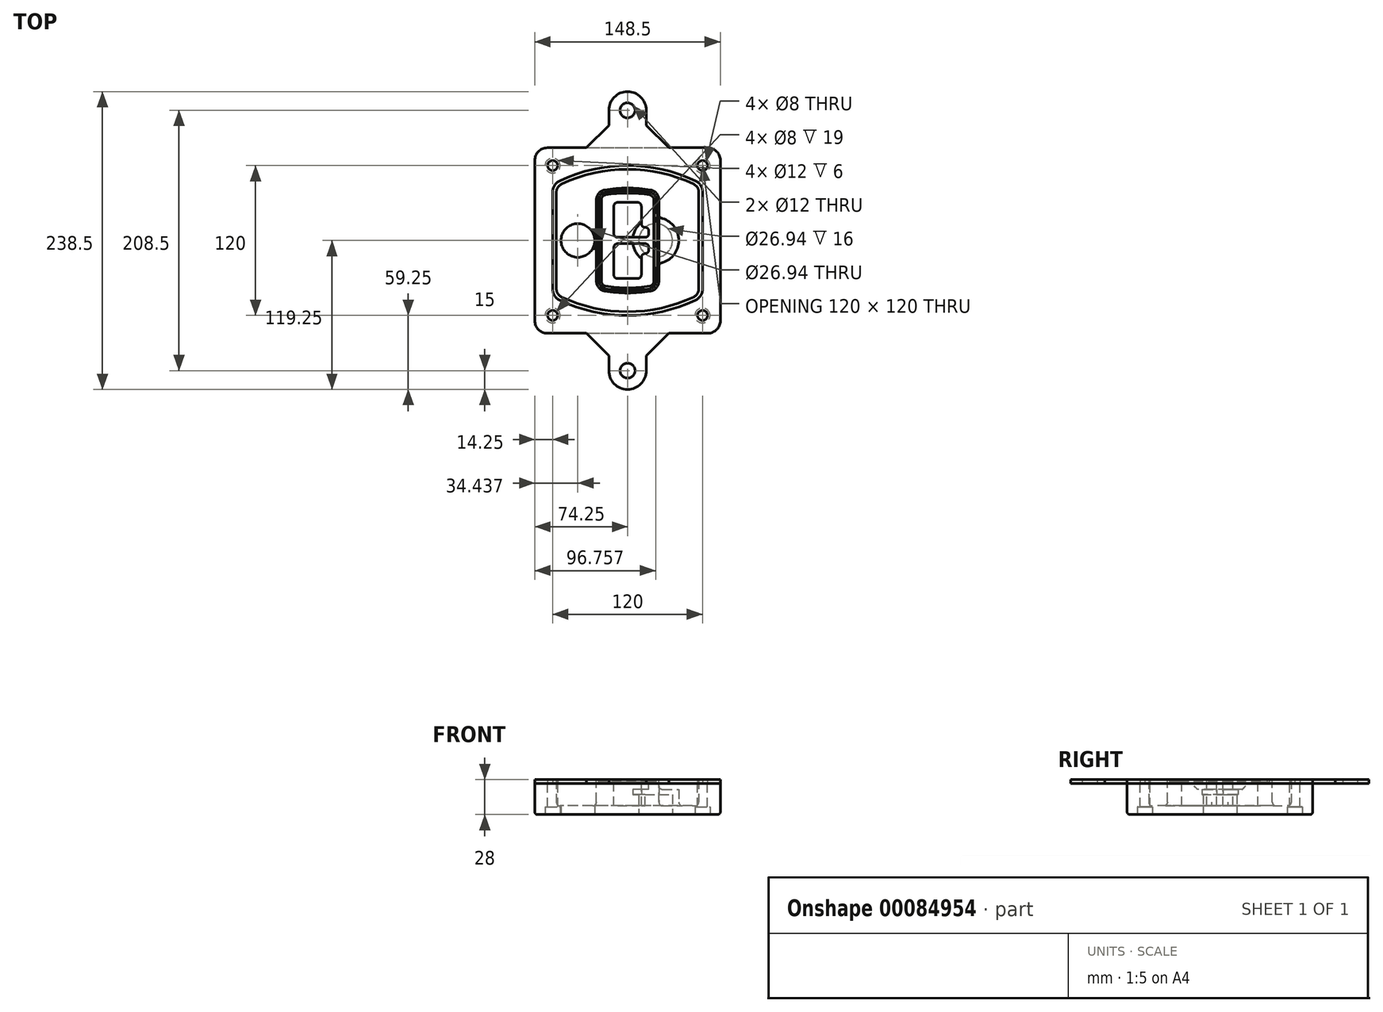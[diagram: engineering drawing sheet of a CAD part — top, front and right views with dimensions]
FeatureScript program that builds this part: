
annotation { "Feature Type Name" : "Feature", "Feature Type Description" : "" }
export const myFeature = defineFeature(function(context is Context, id is Id, definition is map)
    precondition{}
    {
        {
            var Q0;
            Q0=qCreatedBy(makeId("Top.planeOp"),FACE);
            var sketch = newSketch(context, id + "F0", { "sketchPlane" : qUnion([Q0])});
            skPoint(sketch, "E0.rect.middle", {"position": v(0, 0) * mm});
            skLineSegment(sketch, "E1.bottom", {"start": v(-64.25, -74.25) * mm, "end": v(64.25, -74.25) * mm});
            skLineSegment(sketch, "E1.top", {"start": v(-64.25, 74.25) * mm, "end": v(64.25, 74.25) * mm});
            skLineSegment(sketch, "E1.left", {"start": v(-74.25, -64.25) * mm, "end": v(-74.25, 64.25) * mm});
            skLineSegment(sketch, "E1.right", {"start": v(74.25, -64.25) * mm, "end": v(74.25, 64.25) * mm});
            skLineSegment(sketch, "E2", {"start": v(-74.25, 74.25) * mm, "end": v(74.25, -74.25) * mm, "construction": true});
            skLineSegment(sketch, "E3", {"start": v(74.25, 74.25) * mm, "end": v(-74.25, -74.25) * mm, "construction": true});
            skCircle(sketch, "E4", {"center": v(-60, 60) * mm, "radius": 4 * mm});
            skCircle(sketch, "E5", {"center": v(60, 60) * mm, "radius": 4 * mm});
            skCircle(sketch, "E6", {"center": v(60, -60) * mm, "radius": 4 * mm});
            skCircle(sketch, "E7", {"center": v(-60, -60) * mm, "radius": 4 * mm});
            skLineSegment(sketch, "E8", {"start": v(-60, 60) * mm, "end": v(60, 60) * mm, "construction": true});
            skLineSegment(sketch, "E9", {"start": v(60, 60) * mm, "end": v(60, -60) * mm, "construction": true});
            skLineSegment(sketch, "E10", {"start": v(60, -60) * mm, "end": v(-60, -60) * mm, "construction": true});
            skLineSegment(sketch, "E11", {"start": v(-60, -60) * mm, "end": v(-60, 60) * mm, "construction": true});
            skLineSegment(sketch, "E12", {"start": v(-60, 38.83) * mm, "end": v(-60, -38.83) * mm});
            skLineSegment(sketch, "E13", {"start": v(60, 38.83) * mm, "end": v(60, -38.83) * mm});
            skArc(sketch, "E14", {"start": v(54.26, 47.88) * mm, "mid": v(0, 60) * mm, "end": v(-54.26, 47.88) * mm});
            skArc(sketch, "E15", {"start": v(-54.26, -47.88) * mm, "mid": v(0, -60) * mm, "end": v(54.26, -47.88) * mm});
            skLineSegment(sketch, "E16", {"start": v(-60, 0) * mm, "end": v(60, 0) * mm, "construction": true});
            skPoint(sketch, "E17.visualSharp", {"position": v(-60, -45) * mm});
            skArc(sketch, "E17.filletArc", {"start": v(-60, -38.83) * mm, "mid": v(-58.44, -44.2) * mm, "end": v(-54.26, -47.88) * mm});
            skPoint(sketch, "E18.visualSharp", {"position": v(-60, 45) * mm});
            skArc(sketch, "E18.filletArc", {"start": v(-54.26, 47.88) * mm, "mid": v(-58.44, 44.2) * mm, "end": v(-60, 38.83) * mm});
            skPoint(sketch, "E19.visualSharp", {"position": v(60, 45) * mm});
            skArc(sketch, "E19.filletArc", {"start": v(60, 38.83) * mm, "mid": v(58.44, 44.2) * mm, "end": v(54.26, 47.88) * mm});
            skPoint(sketch, "E20.visualSharp", {"position": v(60, -45) * mm});
            skArc(sketch, "E20.filletArc", {"start": v(54.26, -47.88) * mm, "mid": v(58.44, -44.2) * mm, "end": v(60, -38.83) * mm});
            skPoint(sketch, "E21.visualSharp", {"position": v(-74.25, 74.25) * mm});
            skArc(sketch, "E21.filletArc", {"start": v(-64.25, 74.25) * mm, "mid": v(-71.32, 71.32) * mm, "end": v(-74.25, 64.25) * mm});
            skPoint(sketch, "E22.visualSharp", {"position": v(74.25, 74.25) * mm});
            skArc(sketch, "E22.filletArc", {"start": v(74.25, 64.25) * mm, "mid": v(71.32, 71.32) * mm, "end": v(64.25, 74.25) * mm});
            skPoint(sketch, "E23.visualSharp", {"position": v(74.25, -74.25) * mm});
            skArc(sketch, "E23.filletArc", {"start": v(64.25, -74.25) * mm, "mid": v(71.32, -71.32) * mm, "end": v(74.25, -64.25) * mm});
            skPoint(sketch, "E24.visualSharp", {"position": v(-74.25, -74.25) * mm});
            skArc(sketch, "E24.filletArc", {"start": v(-74.25, -64.25) * mm, "mid": v(-71.32, -71.32) * mm, "end": v(-64.25, -74.25) * mm});
            skArc(sketch, "E25.0", {"start": v(57, 38.83) * mm, "mid": v(55.9, 42.58) * mm, "end": v(52.98, 45.17) * mm});
            skLineSegment(sketch, "E25.1", {"start": v(57, 38.83) * mm, "end": v(57, -38.83) * mm});
            skArc(sketch, "E25.2", {"start": v(52.98, -45.17) * mm, "mid": v(55.9, -42.58) * mm, "end": v(57, -38.83) * mm});
            skArc(sketch, "E25.3", {"start": v(-52.98, -45.17) * mm, "mid": v(0, -57) * mm, "end": v(52.98, -45.17) * mm});
            skArc(sketch, "E25.4", {"start": v(-57, -38.83) * mm, "mid": v(-55.9, -42.58) * mm, "end": v(-52.98, -45.17) * mm});
            skArc(sketch, "E25.5", {"start": v(52.98, 45.17) * mm, "mid": v(0, 57) * mm, "end": v(-52.98, 45.17) * mm});
            skLineSegment(sketch, "E25.6", {"start": v(-57, 38.83) * mm, "end": v(-57, -38.83) * mm});
            skArc(sketch, "E25.7", {"start": v(-52.98, 45.17) * mm, "mid": v(-55.9, 42.58) * mm, "end": v(-57, 38.83) * mm});
            skArc(sketch, "E26.0", {"start": v(-55.96, 51.5) * mm, "mid": v(-61.82, 46.33) * mm, "end": v(-64, 38.83) * mm});
            skArc(sketch, "E26.1", {"start": v(55.96, 51.5) * mm, "mid": v(0, 64) * mm, "end": v(-55.96, 51.5) * mm});
            skArc(sketch, "E26.2", {"start": v(64, 38.83) * mm, "mid": v(61.82, 46.33) * mm, "end": v(55.96, 51.5) * mm});
            skLineSegment(sketch, "E26.3", {"start": v(64, 38.83) * mm, "end": v(64, -38.83) * mm});
            skArc(sketch, "E26.4", {"start": v(55.96, -51.5) * mm, "mid": v(61.82, -46.33) * mm, "end": v(64, -38.83) * mm});
            skLineSegment(sketch, "E26.5", {"start": v(-64, 38.83) * mm, "end": v(-64, -38.83) * mm});
            skArc(sketch, "E26.6", {"start": v(-55.96, -51.5) * mm, "mid": v(0, -64) * mm, "end": v(55.96, -51.5) * mm});
            skArc(sketch, "E26.7", {"start": v(-64, -38.83) * mm, "mid": v(-61.82, -46.33) * mm, "end": v(-55.96, -51.5) * mm});
            skSolve(sketch);
        }
        {
            var Q0;
            Q0=makeQuery(id+"F0.imprint","IMPRINT",FACE,{"disambiguationData":[TD([[makeQuery(id+"F0.imprint","IMPRINT",EDGE,{"derivedFrom":sQuery(id+"F0.wireOp",EDGE,"E1.bottom")}),1.0]])]});
            var Q1;
            Q1=makeQuery(id+"F0.imprint","IMPRINT",FACE,{"disambiguationData":[TD([[makeQuery(id+"F0.imprint","IMPRINT",EDGE,{"derivedFrom":sQuery(id+"F0.wireOp",EDGE,"E12")}),1.0]])]});
            var Q2;
            Q2=makeQuery(id+"F0.imprint","IMPRINT",FACE,{"disambiguationData":[TD([[makeQuery(id+"F0.imprint","IMPRINT",EDGE,{"derivedFrom":sQuery(id+"F0.wireOp",EDGE,"E25.0")}),1.0]])]});
            var Q3;
            Q3=makeQuery(id+"F0.imprint","IMPRINT",FACE,{"disambiguationData":[TD([[makeQuery(id+"F0.imprint","IMPRINT",EDGE,{"derivedFrom":sQuery(id+"F0.wireOp",EDGE,"E12")}),-1.0]])]});
            extrude(context, id + "F1", {"entities" : qUnion([Q0, Q1, Q2, Q3]), "oppositeDirection" : true, "depth" : 25 * mm});
        }
        {
            var Q0;
            Q0=makeQuery(id+"F0.imprint","IMPRINT",FACE,{"disambiguationData":[TD([[makeQuery(id+"F0.imprint","IMPRINT",EDGE,{"derivedFrom":sQuery(id+"F0.wireOp",EDGE,"E12")}),1.0]])]});
            extrude(context, id + "F2", {"entities" : qUnion([Q0]), "operationType" : NewBodyOperationType.ADD, "depth" : 3 * mm});
        }
        {
            var Q0;
            Q0=makeQuery(id+"F0.imprint","IMPRINT",FACE,{"disambiguationData":[TD([[makeQuery(id+"F0.imprint","IMPRINT",EDGE,{"derivedFrom":sQuery(id+"F0.wireOp",EDGE,"E25.0")}),1.0]])]});
            extrude(context, id + "F3", {"entities" : qUnion([Q0]), "operationType" : NewBodyOperationType.REMOVE, "oppositeDirection" : true, "depth" : 18 * mm});
        }
        {
            var Q0;
            Q0=makeQuery(id+"F2.opExtrude","CAP_FACE",FACE,{"disambiguationData":[OSD([sQuery(id+"F0.wireOp",EDGE,"E12"),sQuery(id+"F0.wireOp",EDGE,"E13"),sQuery(id+"F0.wireOp",EDGE,"E14"),sQuery(id+"F0.wireOp",EDGE,"E15"),sQuery(id+"F0.wireOp",EDGE,"E17.filletArc"),sQuery(id+"F0.wireOp",EDGE,"E18.filletArc"),sQuery(id+"F0.wireOp",EDGE,"E19.filletArc"),sQuery(id+"F0.wireOp",EDGE,"E20.filletArc"),sQuery(id+"F0.wireOp",EDGE,"E25.0"),sQuery(id+"F0.wireOp",EDGE,"E25.1"),sQuery(id+"F0.wireOp",EDGE,"E25.2"),sQuery(id+"F0.wireOp",EDGE,"E25.3"),sQuery(id+"F0.wireOp",EDGE,"E25.4"),sQuery(id+"F0.wireOp",EDGE,"E25.5"),sQuery(id+"F0.wireOp",EDGE,"E25.6"),sQuery(id+"F0.wireOp",EDGE,"E25.7")])],"isStart":false});
            var sketch = newSketch(context, id + "F4", { "sketchPlane" : qUnion([Q0])});
            skArc(sketch, "E27.0", {"start": v(-18.34, -40.45) * mm, "mid": v(0, -42) * mm, "end": v(18.34, -40.45) * mm});
            skArc(sketch, "E28.0", {"start": v(18.34, 40.45) * mm, "mid": v(0, 42) * mm, "end": v(-18.34, 40.45) * mm});
            skLineSegment(sketch, "E29", {"start": v(-25, 32.57) * mm, "end": v(-25, -32.57) * mm});
            skLineSegment(sketch, "E30", {"start": v(25, 32.57) * mm, "end": v(25, -32.57) * mm});
            skLineSegment(sketch, "E31", {"start": v(-25, 39.1) * mm, "end": v(25, 39.1) * mm, "construction": true});
            skLineSegment(sketch, "E32", {"start": v(-25, -39.1) * mm, "end": v(25, -39.1) * mm, "construction": true});
            skPoint(sketch, "E33.visualSharp", {"position": v(-25, 39.1) * mm});
            skArc(sketch, "E33.filletArc", {"start": v(-18.34, 40.45) * mm, "mid": v(-23.11, 37.73) * mm, "end": v(-25, 32.57) * mm});
            skPoint(sketch, "E34.visualSharp", {"position": v(25, 39.1) * mm});
            skArc(sketch, "E34.filletArc", {"start": v(25, 32.57) * mm, "mid": v(23.11, 37.73) * mm, "end": v(18.34, 40.45) * mm});
            skPoint(sketch, "E35.visualSharp", {"position": v(25, -39.1) * mm});
            skArc(sketch, "E35.filletArc", {"start": v(18.34, -40.45) * mm, "mid": v(23.11, -37.73) * mm, "end": v(25, -32.57) * mm});
            skPoint(sketch, "E36.visualSharp", {"position": v(-25, -39.1) * mm});
            skArc(sketch, "E36.filletArc", {"start": v(-25, -32.57) * mm, "mid": v(-23.11, -37.73) * mm, "end": v(-18.34, -40.45) * mm});
            skArc(sketch, "E37.0", {"start": v(52.98, 45.17) * mm, "mid": v(0, 57) * mm, "end": v(-52.98, 45.17) * mm});
            skArc(sketch, "E37.1", {"start": v(-52.98, 45.17) * mm, "mid": v(-55.9, 42.58) * mm, "end": v(-57, 38.83) * mm});
            skLineSegment(sketch, "E37.2", {"start": v(-57, 38.83) * mm, "end": v(-57, -38.83) * mm});
            skArc(sketch, "E37.3", {"start": v(-57, -38.83) * mm, "mid": v(-55.9, -42.58) * mm, "end": v(-52.98, -45.17) * mm});
            skArc(sketch, "E37.4", {"start": v(-52.98, -45.17) * mm, "mid": v(0, -57) * mm, "end": v(52.98, -45.17) * mm});
            skArc(sketch, "E37.5", {"start": v(52.98, -45.17) * mm, "mid": v(55.9, -42.58) * mm, "end": v(57, -38.83) * mm});
            skLineSegment(sketch, "E37.6", {"start": v(57, 38.83) * mm, "end": v(57, -38.83) * mm});
            skArc(sketch, "E37.7", {"start": v(57, 38.83) * mm, "mid": v(55.9, 42.58) * mm, "end": v(52.98, 45.17) * mm});
            skLineSegment(sketch, "E38.0", {"start": v(23, 32.57) * mm, "end": v(23, -32.57) * mm});
            skArc(sketch, "E38.1", {"start": v(18, -38.48) * mm, "mid": v(21.58, -36.44) * mm, "end": v(23, -32.57) * mm});
            skArc(sketch, "E38.2", {"start": v(-18, -38.48) * mm, "mid": v(0, -40) * mm, "end": v(18, -38.48) * mm});
            skArc(sketch, "E38.3", {"start": v(-23, -32.57) * mm, "mid": v(-21.58, -36.44) * mm, "end": v(-18, -38.48) * mm});
            skLineSegment(sketch, "E38.4", {"start": v(-23, 32.57) * mm, "end": v(-23, -32.57) * mm});
            skArc(sketch, "E38.5", {"start": v(23, 32.57) * mm, "mid": v(21.58, 36.44) * mm, "end": v(18, 38.48) * mm});
            skArc(sketch, "E38.6", {"start": v(-18, 38.48) * mm, "mid": v(-21.58, 36.44) * mm, "end": v(-23, 32.57) * mm});
            skArc(sketch, "E38.7", {"start": v(18, 38.48) * mm, "mid": v(0, 40) * mm, "end": v(-18, 38.48) * mm});
            skArc(sketch, "E39.0", {"start": v(21, 32.57) * mm, "mid": v(20.06, 35.15) * mm, "end": v(17.67, 36.5) * mm});
            skLineSegment(sketch, "E39.1", {"start": v(21, 32.57) * mm, "end": v(21, -32.57) * mm});
            skArc(sketch, "E39.2", {"start": v(17.67, -36.5) * mm, "mid": v(20.06, -35.15) * mm, "end": v(21, -32.57) * mm});
            skArc(sketch, "E39.3", {"start": v(-17.67, -36.5) * mm, "mid": v(0, -38) * mm, "end": v(17.67, -36.5) * mm});
            skArc(sketch, "E39.4", {"start": v(-21, -32.57) * mm, "mid": v(-20.06, -35.15) * mm, "end": v(-17.67, -36.5) * mm});
            skArc(sketch, "E39.5", {"start": v(17.67, 36.5) * mm, "mid": v(0, 38) * mm, "end": v(-17.67, 36.5) * mm});
            skLineSegment(sketch, "E39.6", {"start": v(-21, 32.57) * mm, "end": v(-21, -32.57) * mm});
            skArc(sketch, "E39.7", {"start": v(-17.67, 36.5) * mm, "mid": v(-20.06, 35.15) * mm, "end": v(-21, 32.57) * mm});
            skLineSegment(sketch, "E40", {"start": v(-25, 0) * mm, "end": v(25, 0) * mm, "construction": true});
            skLineSegment(sketch, "E41", {"start": v(-11, 5.5) * mm, "end": v(-11, 27.5) * mm});
            skLineSegment(sketch, "E42", {"start": v(-8, 30.5) * mm, "end": v(8, 30.5) * mm});
            skLineSegment(sketch, "E43", {"start": v(11, 27.5) * mm, "end": v(11, 13.5) * mm});
            skLineSegment(sketch, "E44", {"start": v(14, 10.5) * mm, "end": v(14, 10.5) * mm});
            skLineSegment(sketch, "E45", {"start": v(17, 7.5) * mm, "end": v(17, 5.5) * mm});
            skLineSegment(sketch, "E46", {"start": v(14, 2.5) * mm, "end": v(-8, 2.5) * mm});
            skPoint(sketch, "E47.visualSharp", {"position": v(-11, 30.5) * mm});
            skArc(sketch, "E47.filletArc", {"start": v(-8, 30.5) * mm, "mid": v(-10.12, 29.62) * mm, "end": v(-11, 27.5) * mm});
            skPoint(sketch, "E48.visualSharp", {"position": v(11, 30.5) * mm});
            skArc(sketch, "E48.filletArc", {"start": v(11, 27.5) * mm, "mid": v(10.12, 29.62) * mm, "end": v(8, 30.5) * mm});
            skPoint(sketch, "E49.visualSharp", {"position": v(11, 10.5) * mm});
            skArc(sketch, "E49.filletArc", {"start": v(11, 13.5) * mm, "mid": v(11.88, 11.38) * mm, "end": v(14, 10.5) * mm});
            skPoint(sketch, "E50.visualSharp", {"position": v(17, 10.5) * mm});
            skArc(sketch, "E50.filletArc", {"start": v(17, 7.5) * mm, "mid": v(16.12, 9.62) * mm, "end": v(14, 10.5) * mm});
            skPoint(sketch, "E51.visualSharp", {"position": v(17, 2.5) * mm});
            skArc(sketch, "E51.filletArc", {"start": v(14, 2.5) * mm, "mid": v(16.12, 3.38) * mm, "end": v(17, 5.5) * mm});
            skPoint(sketch, "E52.visualSharp", {"position": v(-11, 2.5) * mm});
            skArc(sketch, "E52.filletArc", {"start": v(-11, 5.5) * mm, "mid": v(-10.12, 3.38) * mm, "end": v(-8, 2.5) * mm});
            skLineSegment(sketch, "E53.0.MirrorCS", {"start": v(14, -2.5) * mm, "end": v(-8, -2.5) * mm});
            skArc(sketch, "E54.0.MirrorCS", {"start": v(-11, -5.5) * mm, "mid": v(-10.12, -3.38) * mm, "end": v(-8, -2.5) * mm});
            skLineSegment(sketch, "E55.0.MirrorCS", {"start": v(-11, -5.5) * mm, "end": v(-11, -27.5) * mm});
            skArc(sketch, "E56.0.MirrorCS", {"start": v(-8, -30.5) * mm, "mid": v(-10.12, -29.62) * mm, "end": v(-11, -27.5) * mm});
            skLineSegment(sketch, "E57.0.MirrorCS", {"start": v(-8, -30.5) * mm, "end": v(8, -30.5) * mm});
            skArc(sketch, "E58.0.MirrorCS", {"start": v(11, -27.5) * mm, "mid": v(10.12, -29.62) * mm, "end": v(8, -30.5) * mm});
            skLineSegment(sketch, "E59.0.MirrorCS", {"start": v(11, -27.5) * mm, "end": v(11, -13.5) * mm});
            skArc(sketch, "E60.0.MirrorCS", {"start": v(11, -13.5) * mm, "mid": v(11.88, -11.38) * mm, "end": v(14, -10.5) * mm});
            skArc(sketch, "E61.0.MirrorCS", {"start": v(17, -7.5) * mm, "mid": v(16.12, -9.62) * mm, "end": v(14, -10.5) * mm});
            skLineSegment(sketch, "E62.0.MirrorCS", {"start": v(17, -7.5) * mm, "end": v(17, -5.5) * mm});
            skArc(sketch, "E63.0.MirrorCS", {"start": v(14, -2.5) * mm, "mid": v(16.12, -3.38) * mm, "end": v(17, -5.5) * mm});
            skSolve(sketch);
        }
        {
            var Q0;
            Q0=makeQuery(id+"F4.imprint","IMPRINT",FACE,{"disambiguationData":[TD([[makeQuery(id+"F4.imprint","IMPRINT",EDGE,{"derivedFrom":sQuery(id+"F4.wireOp",EDGE,"E27.0")}),1.0]])]});
            var Q1;
            Q1=makeQuery(id+"F4.imprint","IMPRINT",FACE,{"disambiguationData":[TD([[makeQuery(id+"F4.imprint","IMPRINT",EDGE,{"derivedFrom":sQuery(id+"F4.wireOp",EDGE,"E38.0")}),-1.0]])]});
            var Q2;
            Q2=makeQuery(id+"F4.imprint","IMPRINT",FACE,{"disambiguationData":[TD([[makeQuery(id+"F4.imprint","IMPRINT",EDGE,{"derivedFrom":sQuery(id+"F4.wireOp",EDGE,"E39.0")}),1.0]])]});
            extrude(context, id + "F5", {"entities" : qUnion([Q0, Q1, Q2]), "operationType" : NewBodyOperationType.ADD, "endBound" : BoundingType.UP_TO_NEXT, "oppositeDirection" : true, "depth" : 25 * mm});
        }
        {
            var Q0;
            Q0=makeQuery(id+"F4.imprint","IMPRINT",FACE,{"disambiguationData":[TD([[makeQuery(id+"F4.imprint","IMPRINT",EDGE,{"derivedFrom":sQuery(id+"F4.wireOp",EDGE,"E38.0")}),-1.0]])]});
            extrude(context, id + "F6", {"entities" : qUnion([Q0]), "operationType" : NewBodyOperationType.REMOVE, "oppositeDirection" : true, "depth" : 2 * mm});
        }
        {
            var Q0;
            Q0=makeQuery(id+"F1.opExtrude","CAP_FACE",FACE,{"disambiguationData":[OSD([sQuery(id+"F0.wireOp",EDGE,"E1.bottom"),sQuery(id+"F0.wireOp",EDGE,"E1.top"),sQuery(id+"F0.wireOp",EDGE,"E1.left"),sQuery(id+"F0.wireOp",EDGE,"E1.right"),sQuery(id+"F0.wireOp",EDGE,"E4"),sQuery(id+"F0.wireOp",EDGE,"E5"),sQuery(id+"F0.wireOp",EDGE,"E6"),sQuery(id+"F0.wireOp",EDGE,"E7"),sQuery(id+"F0.wireOp",EDGE,"E21.filletArc"),sQuery(id+"F0.wireOp",EDGE,"E22.filletArc"),sQuery(id+"F0.wireOp",EDGE,"E23.filletArc"),sQuery(id+"F0.wireOp",EDGE,"E24.filletArc")])],"isStart":false});
            var sketch = newSketch(context, id + "F7", { "sketchPlane" : qUnion([Q0])});
            skCircle(sketch, "E64", {"center": v(22.5, 0) * mm, "radius": 13.47 * mm});
            skCircle(sketch, "E65", {"center": v(-39.81, 0) * mm, "radius": 13.47 * mm});
            skLineSegment(sketch, "E66", {"start": v(74.25, 0) * mm, "end": v(-74.25, 0) * mm});
            skCircle(sketch, "E67", {"center": v(22.5, 0) * mm, "radius": 18.47 * mm});
            skCircle(sketch, "E68", {"center": v(60, -60) * mm, "radius": 6 * mm});
            skCircle(sketch, "E69", {"center": v(-60, -60) * mm, "radius": 6 * mm});
            skCircle(sketch, "E70", {"center": v(-60, 60) * mm, "radius": 6 * mm});
            skCircle(sketch, "E71", {"center": v(60, 60) * mm, "radius": 6 * mm});
            skSolve(sketch);
        }
        {
            var Q0;
            {var subQ1=sQuery(id+"F7.wireOp",EDGE,"E66");var subQ4=sQuery(id+"F7.wireOp",EDGE,"E64");var subQ6=makeQuery(id+"F7.imprint","INTERSECT",VERTEX,{"disambiguationData":[OD(0.0)],"derivedFrom":[subQ4,subQ1]});Q0=makeQuery(id+"F7.imprint","IMPRINT",FACE,{"disambiguationData":[TD([[makeQuery(id+"F7.imprint","IMPRINT",EDGE,{"disambiguationData":[TD([[subQ6,-1.0]])],"derivedFrom":subQ4}),-1.0]])]});}
            var Q1;
            {var subQ0=sQuery(id+"F7.wireOp",EDGE,"E66");var subQ1=sQuery(id+"F7.wireOp",EDGE,"E64");var subQ3=makeQuery(id+"F7.imprint","INTERSECT",VERTEX,{"disambiguationData":[OD(0.0)],"derivedFrom":[subQ1,subQ0]});Q1=makeQuery(id+"F7.imprint","IMPRINT",FACE,{"disambiguationData":[TD([[makeQuery(id+"F7.imprint","IMPRINT",EDGE,{"disambiguationData":[TD([[subQ3,-1.0]])],"derivedFrom":subQ1}),1.0]])]});}
            var Q2;
            {var subQ0=sQuery(id+"F7.wireOp",EDGE,"E66");var subQ1=sQuery(id+"F7.wireOp",EDGE,"E64");var subQ3=makeQuery(id+"F7.imprint","INTERSECT",VERTEX,{"disambiguationData":[OD(0.0)],"derivedFrom":[subQ1,subQ0]});Q2=makeQuery(id+"F7.imprint","IMPRINT",FACE,{"disambiguationData":[TD([[makeQuery(id+"F7.imprint","IMPRINT",EDGE,{"disambiguationData":[TD([[subQ3,1.0]])],"derivedFrom":subQ1}),1.0]])]});}
            var Q3;
            {var subQ1=sQuery(id+"F7.wireOp",EDGE,"E66");var subQ4=sQuery(id+"F7.wireOp",EDGE,"E64");var subQ6=makeQuery(id+"F7.imprint","INTERSECT",VERTEX,{"disambiguationData":[OD(0.0)],"derivedFrom":[subQ4,subQ1]});Q3=makeQuery(id+"F7.imprint","IMPRINT",FACE,{"disambiguationData":[TD([[makeQuery(id+"F7.imprint","IMPRINT",EDGE,{"disambiguationData":[TD([[subQ6,1.0]])],"derivedFrom":subQ4}),-1.0]])]});}
            extrude(context, id + "F8", {"entities" : qUnion([Q0, Q1, Q2, Q3]), "operationType" : NewBodyOperationType.ADD, "oppositeDirection" : true, "depth" : 20 * mm});
        }
        {
            var Q0;
            {var subQ0=sQuery(id+"F7.wireOp",EDGE,"E66");var subQ1=sQuery(id+"F7.wireOp",EDGE,"E64");var subQ3=makeQuery(id+"F7.imprint","INTERSECT",VERTEX,{"disambiguationData":[OD(0.0)],"derivedFrom":[subQ1,subQ0]});Q0=makeQuery(id+"F7.imprint","IMPRINT",FACE,{"disambiguationData":[TD([[makeQuery(id+"F7.imprint","IMPRINT",EDGE,{"disambiguationData":[TD([[subQ3,-1.0]])],"derivedFrom":subQ1}),1.0]])]});}
            var Q1;
            {var subQ0=sQuery(id+"F7.wireOp",EDGE,"E66");var subQ1=sQuery(id+"F7.wireOp",EDGE,"E64");var subQ3=makeQuery(id+"F7.imprint","INTERSECT",VERTEX,{"disambiguationData":[OD(0.0)],"derivedFrom":[subQ1,subQ0]});Q1=makeQuery(id+"F7.imprint","IMPRINT",FACE,{"disambiguationData":[TD([[makeQuery(id+"F7.imprint","IMPRINT",EDGE,{"disambiguationData":[TD([[subQ3,1.0]])],"derivedFrom":subQ1}),1.0]])]});}
            extrude(context, id + "F9", {"entities" : qUnion([Q0, Q1]), "operationType" : NewBodyOperationType.REMOVE, "oppositeDirection" : true, "depth" : 16 * mm});
        }
        {
            var Q0;
            {var subQ0=sQuery(id+"F7.wireOp",EDGE,"E66");var subQ1=sQuery(id+"F7.wireOp",EDGE,"E65");var subQ3=makeQuery(id+"F7.imprint","INTERSECT",VERTEX,{"disambiguationData":[OD(0.0)],"derivedFrom":[subQ1,subQ0]});Q0=makeQuery(id+"F7.imprint","IMPRINT",FACE,{"disambiguationData":[TD([[makeQuery(id+"F7.imprint","IMPRINT",EDGE,{"disambiguationData":[TD([[subQ3,-1.0]])],"derivedFrom":subQ1}),1.0]])]});}
            var Q1;
            {var subQ0=sQuery(id+"F7.wireOp",EDGE,"E66");var subQ1=sQuery(id+"F7.wireOp",EDGE,"E65");var subQ3=makeQuery(id+"F7.imprint","INTERSECT",VERTEX,{"disambiguationData":[OD(0.0)],"derivedFrom":[subQ1,subQ0]});Q1=makeQuery(id+"F7.imprint","IMPRINT",FACE,{"disambiguationData":[TD([[makeQuery(id+"F7.imprint","IMPRINT",EDGE,{"disambiguationData":[TD([[subQ3,1.0]])],"derivedFrom":subQ1}),1.0]])]});}
            extrude(context, id + "F10", {"entities" : qUnion([Q0, Q1]), "operationType" : NewBodyOperationType.REMOVE, "oppositeDirection" : true, "depth" : 25 * mm});
        }
        {
            var Q0;
            Q0=makeQuery(id+"F7.imprint","IMPRINT",FACE,{"disambiguationData":[TD([[makeQuery(id+"F7.imprint","IMPRINT",EDGE,{"derivedFrom":sQuery(id+"F7.wireOp",EDGE,"E68")}),1.0]])]});
            var Q1;
            Q1=makeQuery(id+"F7.imprint","IMPRINT",FACE,{"disambiguationData":[TD([[makeQuery(id+"F7.imprint","IMPRINT",EDGE,{"derivedFrom":makeQuery(id+"F1.opExtrude","CAP_EDGE",EDGE,{"disambiguationData":[OSD([sQuery(id+"F0.wireOp",EDGE,"E5")])],"isStart":false})}),-1.0]])]});
            var Q2;
            Q2=makeQuery(id+"F7.imprint","IMPRINT",FACE,{"disambiguationData":[TD([[makeQuery(id+"F7.imprint","IMPRINT",EDGE,{"derivedFrom":sQuery(id+"F7.wireOp",EDGE,"E69")}),1.0]])]});
            var Q3;
            Q3=makeQuery(id+"F7.imprint","IMPRINT",FACE,{"disambiguationData":[TD([[makeQuery(id+"F7.imprint","IMPRINT",EDGE,{"derivedFrom":makeQuery(id+"F1.opExtrude","CAP_EDGE",EDGE,{"disambiguationData":[OSD([sQuery(id+"F0.wireOp",EDGE,"E4")])],"isStart":false})}),-1.0]])]});
            var Q4;
            Q4=makeQuery(id+"F7.imprint","IMPRINT",FACE,{"disambiguationData":[TD([[makeQuery(id+"F7.imprint","IMPRINT",EDGE,{"derivedFrom":sQuery(id+"F7.wireOp",EDGE,"E70")}),1.0]])]});
            var Q5;
            Q5=makeQuery(id+"F7.imprint","IMPRINT",FACE,{"disambiguationData":[TD([[makeQuery(id+"F7.imprint","IMPRINT",EDGE,{"derivedFrom":makeQuery(id+"F1.opExtrude","CAP_EDGE",EDGE,{"disambiguationData":[OSD([sQuery(id+"F0.wireOp",EDGE,"E7")])],"isStart":false})}),-1.0]])]});
            var Q6;
            Q6=makeQuery(id+"F7.imprint","IMPRINT",FACE,{"disambiguationData":[TD([[makeQuery(id+"F7.imprint","IMPRINT",EDGE,{"derivedFrom":sQuery(id+"F7.wireOp",EDGE,"E71")}),1.0]])]});
            var Q7;
            Q7=makeQuery(id+"F7.imprint","IMPRINT",FACE,{"disambiguationData":[TD([[makeQuery(id+"F7.imprint","IMPRINT",EDGE,{"derivedFrom":makeQuery(id+"F1.opExtrude","CAP_EDGE",EDGE,{"disambiguationData":[OSD([sQuery(id+"F0.wireOp",EDGE,"E6")])],"isStart":false})}),-1.0]])]});
            extrude(context, id + "F11", {"entities" : qUnion([Q0, Q1, Q2, Q3, Q4, Q5, Q6, Q7]), "operationType" : NewBodyOperationType.REMOVE, "oppositeDirection" : true, "depth" : 6 * mm});
        }
        {
            var Q0;
            Q0=makeQuery(id+"F9.boolean.opBoolean","COPY",FACE,{"derivedFrom":makeQuery(id+"F9.opExtrude","CAP_FACE",FACE,{"disambiguationData":[OSD([sQuery(id+"F7.wireOp",EDGE,"E64")])],"isStart":false})});
            var sketch = newSketch(context, id + "F12", { "sketchPlane" : qUnion([Q0])});
            skArc(sketch, "E72.0", {"start": v(11, 14.45) * mm, "mid": v(6.45, 9.13) * mm, "end": v(4.2, 2.5) * mm});
            skArc(sketch, "E72.1", {"start": v(4.2, -2.5) * mm, "mid": v(6.45, -9.13) * mm, "end": v(11, -14.45) * mm});
            skLineSegment(sketch, "E73", {"start": v(4.2, -2.5) * mm, "end": v(14, -2.5) * mm});
            skLineSegment(sketch, "E74.0", {"start": v(14, 2.5) * mm, "end": v(4.2, 2.5) * mm});
            skArc(sketch, "E74.1", {"start": v(14, 2.5) * mm, "mid": v(16.12, 3.38) * mm, "end": v(17, 5.5) * mm});
            skLineSegment(sketch, "E74.2", {"start": v(17, 7.5) * mm, "end": v(17, 5.5) * mm});
            skArc(sketch, "E74.3", {"start": v(17, 7.5) * mm, "mid": v(16.12, 9.62) * mm, "end": v(14, 10.5) * mm});
            skArc(sketch, "E74.4", {"start": v(11, 13.5) * mm, "mid": v(11.88, 11.38) * mm, "end": v(14, 10.5) * mm});
            skLineSegment(sketch, "E74.5", {"start": v(11, 14.45) * mm, "end": v(11, 13.5) * mm});
            skLineSegment(sketch, "E74.7", {"start": v(14, -2.5) * mm, "end": v(4.2, -2.5) * mm});
            skArc(sketch, "E74.8", {"start": v(14, -2.5) * mm, "mid": v(16.12, -3.38) * mm, "end": v(17, -5.5) * mm});
            skLineSegment(sketch, "E74.9", {"start": v(17, -7.5) * mm, "end": v(17, -5.5) * mm});
            skArc(sketch, "E74.10", {"start": v(17, -7.5) * mm, "mid": v(16.12, -9.62) * mm, "end": v(14, -10.5) * mm});
            skArc(sketch, "E74.11", {"start": v(11, -13.5) * mm, "mid": v(11.88, -11.38) * mm, "end": v(14, -10.5) * mm});
            skLineSegment(sketch, "E74.12", {"start": v(11, -14.45) * mm, "end": v(11, -13.5) * mm});
            skPoint(sketch, "E75.orphan", {"position": v(11, -27.5) * mm});
            skPoint(sketch, "E76.orphan", {"position": v(-8, -2.5) * mm});
            skPoint(sketch, "E77.orphan", {"position": v(-8, 2.5) * mm});
            skPoint(sketch, "E78.orphan", {"position": v(11, 27.5) * mm});
            skSolve(sketch);
        }
        {
            var Q0;
            {var subQ7=sQuery(id+"F12.wireOp",EDGE,"E72.0");var subQ14=sQuery(id+"F12.wireOp",EDGE,"E72.1");var subQ16=sQuery(id+"F12.wireOp",EDGE,"E74.1");var subQ18=sQuery(id+"F12.wireOp",EDGE,"E74.8");Q0=qUnion([makeQuery(id+"F12.imprint","IMPRINT",FACE,{"disambiguationData":[TD([[makeQuery(id+"F12.imprint","IMPRINT",EDGE,{"derivedFrom":subQ7}),1.0]])]}),makeQuery(id+"F12.imprint","IMPRINT",FACE,{"disambiguationData":[TD([[makeQuery(id+"F12.imprint","IMPRINT",EDGE,{"derivedFrom":subQ14}),1.0]])]}),makeQuery(id+"F12.imprint","IMPRINT",FACE,{"disambiguationData":[TD([[makeQuery(id+"F12.imprint","IMPRINT",EDGE,{"derivedFrom":subQ16}),1.0]])]}),makeQuery(id+"F12.imprint","IMPRINT",FACE,{"disambiguationData":[TD([[makeQuery(id+"F12.imprint","IMPRINT",EDGE,{"derivedFrom":subQ18}),-1.0]])]})]);}
            var Q1;
            Q1=makeQuery(id+"F5.boolean.opBoolean","SPLIT",FACE,{"disambiguationData":[TD([makeQuery(id+"F5.opExtrude","SWEPT_FACE",FACE,{"disambiguationData":[OSD([sQuery(id+"F4.wireOp",EDGE,"E41")])]})])],"derivedFrom":makeQuery(id+"F3.boolean.opBoolean","COPY",FACE,{"derivedFrom":makeQuery(id+"F3.opExtrude","CAP_FACE",FACE,{"disambiguationData":[OSD([sQuery(id+"F0.wireOp",EDGE,"E25.0"),sQuery(id+"F0.wireOp",EDGE,"E25.1"),sQuery(id+"F0.wireOp",EDGE,"E25.2"),sQuery(id+"F0.wireOp",EDGE,"E25.3"),sQuery(id+"F0.wireOp",EDGE,"E25.4"),sQuery(id+"F0.wireOp",EDGE,"E25.5"),sQuery(id+"F0.wireOp",EDGE,"E25.6"),sQuery(id+"F0.wireOp",EDGE,"E25.7")])],"isStart":false})})});
            extrude(context, id + "F13", {"entities" : qUnion([Q0]), "operationType" : NewBodyOperationType.REMOVE, "endBound" : BoundingType.UP_TO_SURFACE, "endBoundEntityFace" : qUnion([Q1]), "depth" : 25 * mm});
        }
        {
            var Q0;
            Q0=makeQuery(id+"F3.boolean.opBoolean","COPY",EDGE,{"derivedFrom":makeQuery(id+"F3.opExtrude","CAP_EDGE",EDGE,{"disambiguationData":[OSD([sQuery(id+"F0.wireOp",EDGE,"E25.6")])],"isStart":false})});
            var Q1;
            Q1=makeQuery(id+"F8.boolean.opBoolean","INTERSECT",EDGE,{"derivedFrom":[makeQuery(id+"F5.opExtrude","SWEPT_FACE",FACE,{"disambiguationData":[OSD([sQuery(id+"F4.wireOp",EDGE,"E30")])]}),makeQuery(id+"F8.opExtrude","CAP_FACE",FACE,{"disambiguationData":[OSD([sQuery(id+"F7.wireOp",EDGE,"E67")])],"isStart":false})]});
            var Q2;
            Q2=makeQuery(id+"F8.boolean.opBoolean","INTERSECT",EDGE,{"disambiguationData":[OD(1.0)],"derivedFrom":[makeQuery(id+"F5.opExtrude","SWEPT_FACE",FACE,{"disambiguationData":[OSD([sQuery(id+"F4.wireOp",EDGE,"E30")])]}),makeQuery(id+"F8.opExtrude","SWEPT_FACE",FACE,{"disambiguationData":[OSD([sQuery(id+"F7.wireOp",EDGE,"E67")])]})]});
            var Q3;
            {var subQ0=sQuery(id+"F4.wireOp",EDGE,"E30");Q3=makeQuery(id+"F8.boolean.opBoolean","SPLIT",EDGE,{"disambiguationData":[TD([makeQuery(id+"F5.opExtrude","SWEPT_FACE",FACE,{"disambiguationData":[OSD([sQuery(id+"F4.wireOp",EDGE,"E35.filletArc")])]})])],"derivedFrom":makeQuery(id+"F5.opExtrude","CAP_EDGE",EDGE,{"disambiguationData":[OSD([subQ0])],"isStart":false})});}
            var Q4;
            {var subQ0=sQuery(id+"F0.wireOp",EDGE,"E25.7");var subQ1=sQuery(id+"F0.wireOp",EDGE,"E25.1");var subQ2=sQuery(id+"F0.wireOp",EDGE,"E25.6");var subQ3=sQuery(id+"F0.wireOp",EDGE,"E25.5");var subQ4=sQuery(id+"F0.wireOp",EDGE,"E25.4");var subQ5=sQuery(id+"F0.wireOp",EDGE,"E25.0");var subQ6=sQuery(id+"F0.wireOp",EDGE,"E25.2");var subQ7=sQuery(id+"F0.wireOp",EDGE,"E25.3");Q4=makeQuery(id+"F8.boolean.opBoolean","INTERSECT",EDGE,{"derivedFrom":[makeQuery(id+"F5.boolean.opBoolean","SPLIT",FACE,{"disambiguationData":[TD([makeQuery(id+"F2.opExtrude","SWEPT_FACE",FACE,{"disambiguationData":[OSD([subQ5])]})])],"derivedFrom":makeQuery(id+"F3.boolean.opBoolean","COPY",FACE,{"derivedFrom":makeQuery(id+"F3.opExtrude","CAP_FACE",FACE,{"disambiguationData":[OSD([subQ5,subQ1,subQ6,subQ7,subQ4,subQ3,subQ2,subQ0])],"isStart":false})})}),makeQuery(id+"F8.opExtrude","SWEPT_FACE",FACE,{"disambiguationData":[OSD([sQuery(id+"F7.wireOp",EDGE,"E67")])]})]});}
            var Q5;
            Q5=makeQuery(id+"F8.boolean.opBoolean","INTERSECT",EDGE,{"disambiguationData":[OD(0.0)],"derivedFrom":[makeQuery(id+"F5.opExtrude","SWEPT_FACE",FACE,{"disambiguationData":[OSD([sQuery(id+"F4.wireOp",EDGE,"E30")])]}),makeQuery(id+"F8.opExtrude","SWEPT_FACE",FACE,{"disambiguationData":[OSD([sQuery(id+"F7.wireOp",EDGE,"E67")])]})]});
            fillet(context, id + "F14", {"entities" : qUnion([Q0, Q1, Q2, Q3, Q4, Q5]), "radius" : 3 * mm, "tangentPropagation" : true, "allowEdgeOverflow" : false});
        }
        {
            var Q0;
            Q0=makeQuery(id+"F1.opExtrude","CAP_EDGE",EDGE,{"disambiguationData":[OSD([sQuery(id+"F0.wireOp",EDGE,"E1.bottom")])],"isStart":false});
            fillet(context, id + "F15", {"entities" : qUnion([Q0]), "radius" : 2 * mm, "tangentPropagation" : true, "allowEdgeOverflow" : false});
        }
        {
            var Q0;
            {var subQ0=sQuery(id+"F0.wireOp",EDGE,"E22.filletArc");var subQ1=sQuery(id+"F0.wireOp",EDGE,"E7");var subQ2=sQuery(id+"F0.wireOp",EDGE,"E6");var subQ3=sQuery(id+"F0.wireOp",EDGE,"E5");var subQ4=sQuery(id+"F0.wireOp",EDGE,"E4");var subQ5=sQuery(id+"F0.wireOp",EDGE,"E1.bottom");var subQ6=sQuery(id+"F0.wireOp",EDGE,"E21.filletArc");var subQ7=sQuery(id+"F0.wireOp",EDGE,"E1.top");var subQ8=sQuery(id+"F0.wireOp",EDGE,"E1.left");var subQ9=sQuery(id+"F0.wireOp",EDGE,"E1.right");var subQ10=sQuery(id+"F0.wireOp",EDGE,"E23.filletArc");var subQ11=sQuery(id+"F0.wireOp",EDGE,"E24.filletArc");Q0=makeQuery(id+"F2.boolean.opBoolean","SPLIT",FACE,{"disambiguationData":[TD([makeQuery(id+"F1.opExtrude","SWEPT_FACE",FACE,{"disambiguationData":[OSD([subQ5])]})])],"derivedFrom":makeQuery(id+"F1.opExtrude","CAP_FACE",FACE,{"disambiguationData":[OSD([subQ5,subQ7,subQ8,subQ9,subQ4,subQ3,subQ2,subQ1,subQ6,subQ0,subQ10,subQ11])],"isStart":true})});}
            var sketch = newSketch(context, id + "F16", { "sketchPlane" : qUnion([Q0])});
            skLineSegment(sketch, "E79", {"start": v(-15, 92.25) * mm, "end": v(-15, 104.25) * mm});
            skLineSegment(sketch, "E80", {"start": v(15, 92.25) * mm, "end": v(15, 104.25) * mm});
            skArc(sketch, "E81", {"start": v(15, 104.25) * mm, "mid": v(0, 119.25) * mm, "end": v(-15, 104.25) * mm});
            skCircle(sketch, "E82", {"center": v(0, 104.25) * mm, "radius": 6 * mm});
            skLineSegment(sketch, "E83", {"start": v(0, 74.25) * mm, "end": v(0, 104.25) * mm, "construction": true});
            skLineSegment(sketch, "E84", {"start": v(-15, 92.25) * mm, "end": v(-33, 74.25) * mm});
            skLineSegment(sketch, "E85", {"start": v(15, 92.25) * mm, "end": v(33, 74.25) * mm});
            skArc(sketch, "E86.MirrorCS", {"start": v(-15, 104.25) * mm, "mid": v(0, 119.25) * mm, "end": v(15, 104.25) * mm});
            skLineSegment(sketch, "E87", {"start": v(-119.6, 0) * mm, "end": v(129.86, 0) * mm, "construction": true});
            skPoint(sketch, "E87.endSnap0", {"position": v(74.25, 0) * mm});
            skLineSegment(sketch, "E88.MirrorCS", {"start": v(-15, -92.25) * mm, "end": v(-33, -74.25) * mm});
            skArc(sketch, "E89.MirrorCS", {"start": v(-15, -104.25) * mm, "mid": v(0, -119.25) * mm, "end": v(15, -104.25) * mm});
            skLineSegment(sketch, "E90.MirrorCS", {"start": v(15, -92.25) * mm, "end": v(15, -104.25) * mm});
            skLineSegment(sketch, "E91.MirrorCS", {"start": v(-15, -92.25) * mm, "end": v(-15, -104.25) * mm});
            skCircle(sketch, "E92.MirrorC", {"center": v(0, -104.25) * mm, "radius": 6 * mm});
            skArc(sketch, "E93.MirrorCS", {"start": v(15, -104.25) * mm, "mid": v(0, -119.25) * mm, "end": v(-15, -104.25) * mm});
            skLineSegment(sketch, "E94.MirrorCS", {"start": v(0, -74.25) * mm, "end": v(0, -104.25) * mm, "construction": true});
            skLineSegment(sketch, "E95.MirrorCS", {"start": v(15, -92.25) * mm, "end": v(33, -74.25) * mm});
            skSolve(sketch);
        }
        {
            var Q0;
            Q0=makeQuery(id+"F16.imprint","IMPRINT",FACE,{"disambiguationData":[TD([[makeQuery(id+"F16.imprint","IMPRINT",EDGE,{"derivedFrom":sQuery(id+"F16.wireOp",EDGE,"E80")}),1.0]])]});
            var Q1;
            Q1=makeQuery(id+"F16.imprint","IMPRINT",FACE,{"disambiguationData":[TD([[makeQuery(id+"F16.imprint","IMPRINT",EDGE,{"derivedFrom":makeQuery(id+"F1.opExtrude","CAP_EDGE",EDGE,{"disambiguationData":[OSD([sQuery(id+"F0.wireOp",EDGE,"E1.left")])],"isStart":true})}),-1.0]])]});
            var Q2;
            Q2=makeQuery(id+"F16.imprint","IMPRINT",FACE,{"disambiguationData":[TD([[makeQuery(id+"F16.imprint","IMPRINT",EDGE,{"derivedFrom":sQuery(id+"F16.wireOp",EDGE,"E91.MirrorCS")}),1.0]])]});
            var Q3;
            Q3=makeQuery(id+"F2.opExtrude","CAP_FACE",FACE,{"disambiguationData":[OSD([sQuery(id+"F0.wireOp",EDGE,"E12"),sQuery(id+"F0.wireOp",EDGE,"E13"),sQuery(id+"F0.wireOp",EDGE,"E14"),sQuery(id+"F0.wireOp",EDGE,"E15"),sQuery(id+"F0.wireOp",EDGE,"E17.filletArc"),sQuery(id+"F0.wireOp",EDGE,"E18.filletArc"),sQuery(id+"F0.wireOp",EDGE,"E19.filletArc"),sQuery(id+"F0.wireOp",EDGE,"E20.filletArc"),sQuery(id+"F0.wireOp",EDGE,"E25.0"),sQuery(id+"F0.wireOp",EDGE,"E25.1"),sQuery(id+"F0.wireOp",EDGE,"E25.2"),sQuery(id+"F0.wireOp",EDGE,"E25.3"),sQuery(id+"F0.wireOp",EDGE,"E25.4"),sQuery(id+"F0.wireOp",EDGE,"E25.5"),sQuery(id+"F0.wireOp",EDGE,"E25.6"),sQuery(id+"F0.wireOp",EDGE,"E25.7")])],"isStart":false});
            extrude(context, id + "F17", {"entities" : qUnion([Q0, Q1, Q2]), "endBound" : BoundingType.UP_TO_SURFACE, "endBoundEntityFace" : qUnion([Q3]), "depth" : 25 * mm});
        }
    });
